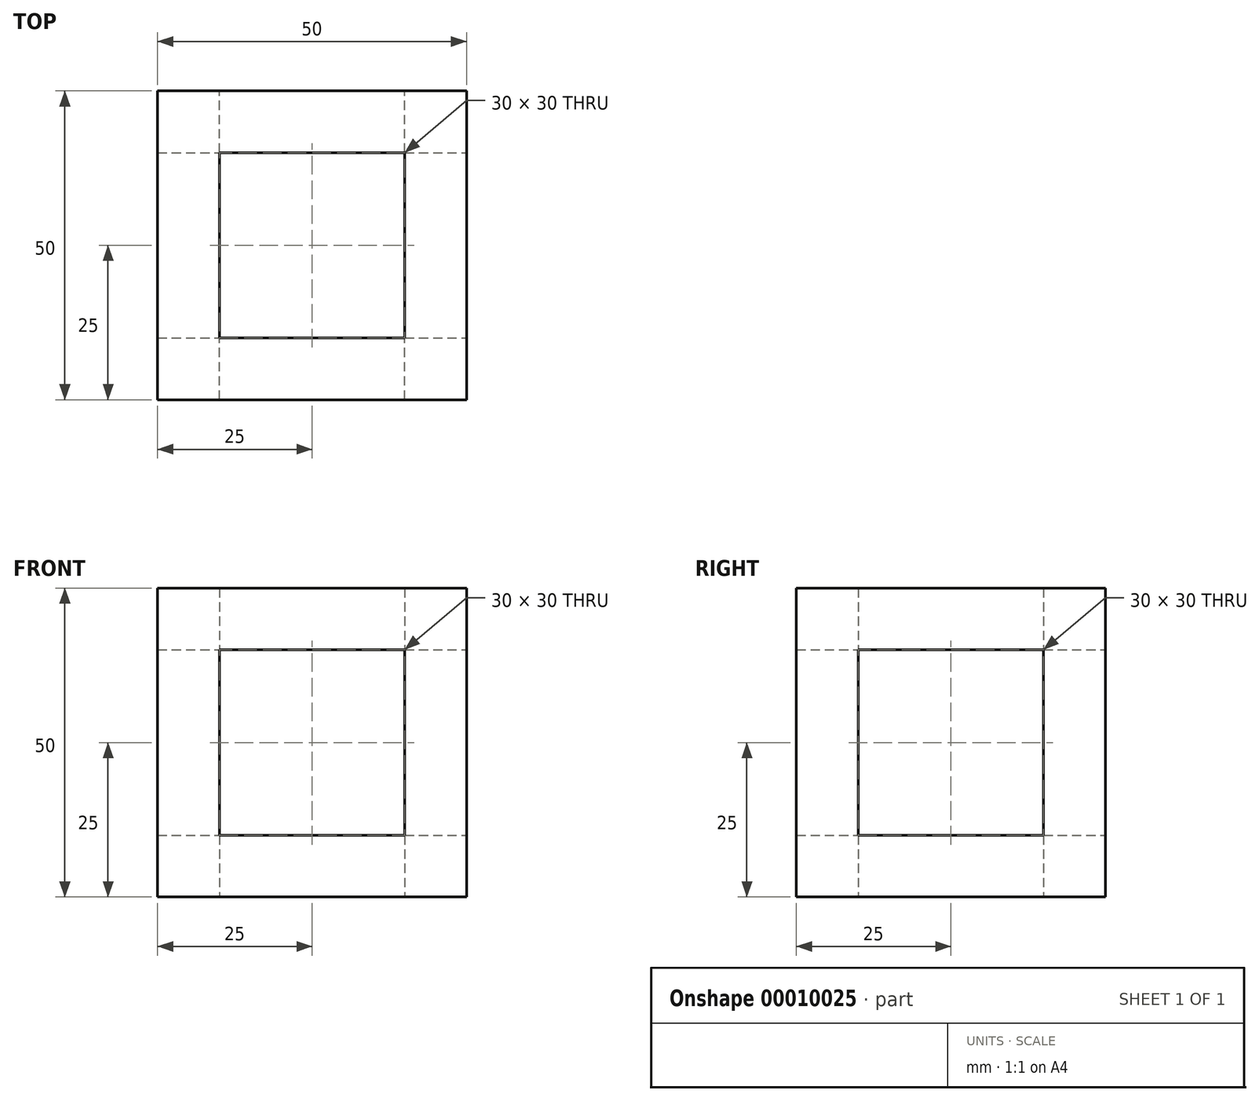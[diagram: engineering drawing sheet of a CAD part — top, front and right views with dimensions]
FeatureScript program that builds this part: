
annotation { "Feature Type Name" : "Feature", "Feature Type Description" : "" }
export const myFeature = defineFeature(function(context is Context, id is Id, definition is map)
    precondition{}
    {
        {
            var Q0;
            Q0=qCreatedBy(makeId("Top.planeOp"),FACE);
            var sketch = newSketch(context, id + "F0", { "sketchPlane" : qUnion([Q0])});
            skLineSegment(sketch, "E0.bottom", {"start": v(0, 0) * mm, "end": v(50, 0) * mm});
            skLineSegment(sketch, "E0.top", {"start": v(0, 50) * mm, "end": v(50, 50) * mm});
            skLineSegment(sketch, "E0.left", {"start": v(0, 0) * mm, "end": v(0, 50) * mm});
            skLineSegment(sketch, "E0.right", {"start": v(50, 0) * mm, "end": v(50, 50) * mm});
            skLineSegment(sketch, "E1.bottom", {"start": v(10, 10) * mm, "end": v(40, 10) * mm});
            skLineSegment(sketch, "E1.top", {"start": v(10, 40) * mm, "end": v(40, 40) * mm});
            skLineSegment(sketch, "E1.left", {"start": v(10, 10) * mm, "end": v(10, 40) * mm});
            skLineSegment(sketch, "E1.right", {"start": v(40, 10) * mm, "end": v(40, 40) * mm});
            skSolve(sketch);
        }
        {
            var Q0;
            Q0 = qSketchRegion(id + "F0", true);
            extrude(context, id + "F1", {"entities" : qUnion([Q0]), "depth" : 50 * mm});
        }
        {
            var Q0;
            Q0 = qSketchRegion(id + "F0", true);
            extrude(context, id + "F2", {"entities" : qUnion([Q0]), "operationType" : NewBodyOperationType.REMOVE, "endBound" : BoundingType.THROUGH_ALL, "oppositeDirection" : true, "depth" : 50 * mm});
        }
        {
            var Q0;
            Q0=makeQuery(id+"F1.opExtrude","SWEPT_FACE",FACE,{"disambiguationData":[OSD([sQuery(id+"F0.wireOp",EDGE,"E0.right")])]});
            var sketch = newSketch(context, id + "F3", { "sketchPlane" : qUnion([Q0])});
            skLineSegment(sketch, "E2.bottom", {"start": v(10, 10) * mm, "end": v(40, 10) * mm});
            skLineSegment(sketch, "E2.top", {"start": v(10, 40) * mm, "end": v(40, 40) * mm});
            skLineSegment(sketch, "E2.left", {"start": v(10, 10) * mm, "end": v(10, 40) * mm});
            skLineSegment(sketch, "E2.right", {"start": v(40, 10) * mm, "end": v(40, 40) * mm});
            skSolve(sketch);
        }
        {
            var Q0;
            Q0=makeQuery(id+"F3.imprint","IMPRINT",FACE,{"disambiguationData":[TD([[makeQuery(id+"F3.imprint","IMPRINT",EDGE,{"derivedFrom":sQuery(id+"F3.wireOp",EDGE,"E2.bottom")}),1.0]])]});
            extrude(context, id + "F4", {"entities" : qUnion([Q0]), "operationType" : NewBodyOperationType.REMOVE, "endBound" : BoundingType.THROUGH_ALL, "oppositeDirection" : true, "depth" : 25.4 * mm});
        }
        {
            var Q0;
            Q0=makeQuery(id+"F1.opExtrude","SWEPT_FACE",FACE,{"disambiguationData":[OSD([sQuery(id+"F0.wireOp",EDGE,"E0.top")])]});
            var sketch = newSketch(context, id + "F5", { "sketchPlane" : qUnion([Q0])});
            skLineSegment(sketch, "E3.bottom", {"start": v(-40, 40) * mm, "end": v(-10, 40) * mm});
            skLineSegment(sketch, "E3.top", {"start": v(-40, 10) * mm, "end": v(-10, 10) * mm});
            skLineSegment(sketch, "E3.left", {"start": v(-40, 40) * mm, "end": v(-40, 10) * mm});
            skLineSegment(sketch, "E3.right", {"start": v(-10, 40) * mm, "end": v(-10, 10) * mm});
            skSolve(sketch);
        }
        {
            var Q0;
            Q0=makeQuery(id+"F5.imprint","IMPRINT",FACE,{"disambiguationData":[TD([[makeQuery(id+"F5.imprint","IMPRINT",EDGE,{"derivedFrom":sQuery(id+"F5.wireOp",EDGE,"E3.bottom")}),-1.0]])]});
            extrude(context, id + "F6", {"entities" : qUnion([Q0]), "operationType" : NewBodyOperationType.REMOVE, "endBound" : BoundingType.THROUGH_ALL, "oppositeDirection" : true, "depth" : 25.4 * mm});
        }
    });
